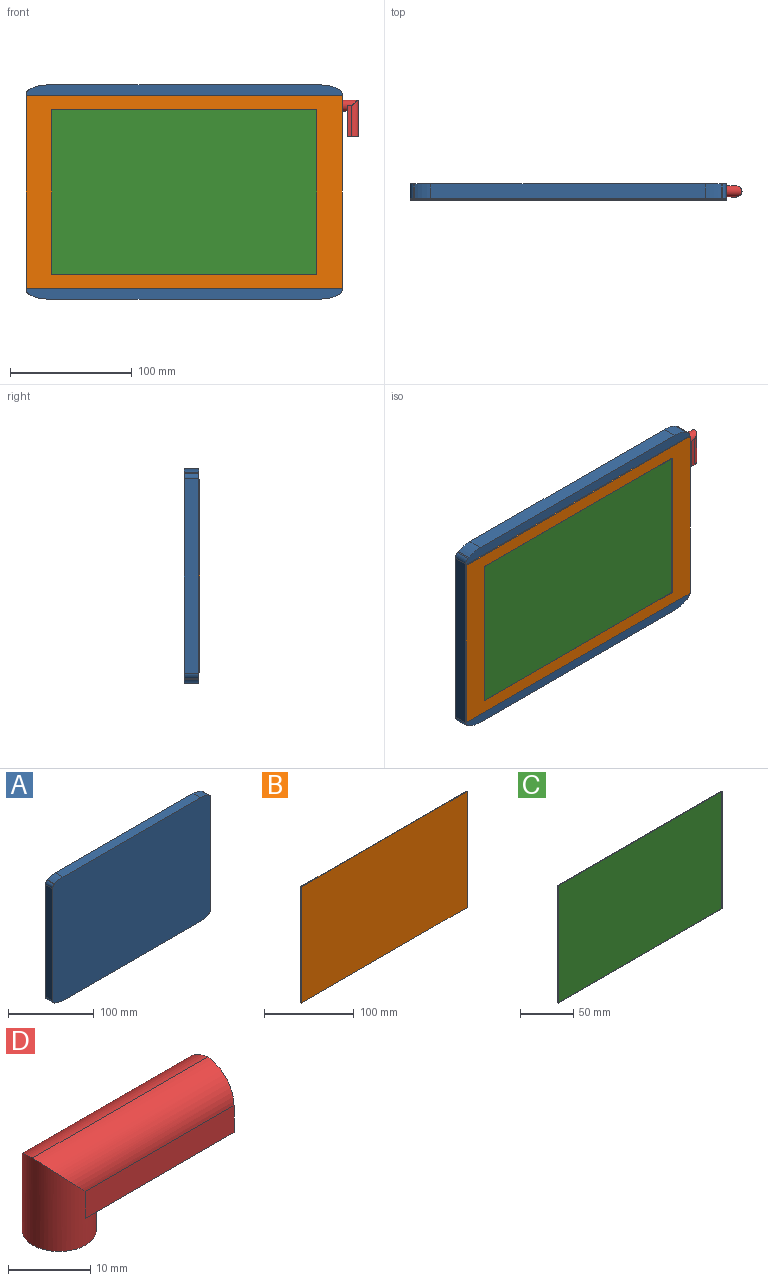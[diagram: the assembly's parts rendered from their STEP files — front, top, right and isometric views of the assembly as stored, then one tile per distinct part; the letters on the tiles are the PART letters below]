
ASSEMBLY  parts=4 mates=3
PART A: 20 faces, bbox 260x12x176 mm
  f0: plane 12x0.9mm, normal (-0.45,0,0.89), area 12.1mm2, adj f8,f9,f10,f17
  f1: plane 159.82x12mm, normal (-1,0,0), area 1917.8mm2, adj f8,f9,f10,f11
  f2: plane 12x0.9mm, normal (-0.45,0,-0.89), area 12.1mm2, adj f8,f9,f11,f14
  f3: plane 225.84x12mm, normal (0,0,-1), area 2710mm2, adj f8,f9,f14,f15
  f4: plane 12x0.9mm, normal (0.45,0,-0.89), area 12.1mm2, adj f8,f9,f12,f15
  f5: plane 159.82x12mm, normal (1,0,0), area 1909.8mm2, adj f8,f9,f12,f13,f19
  f6: plane 12x0.9mm, normal (0.45,0,0.89), area 12.1mm2, adj f8,f9,f13,f16
  f7: plane 225.84x12mm, normal (0,0,1), area 2710mm2, adj f8,f9,f16,f17
  f8: plane 260x176mm, normal (0,-1,0), area 45638.3mm2, adj f0,f1,f2,f3,f4,f5,f6,f7
  f9: plane 260x176mm, normal (0,1,0), area 45638.3mm2, adj f0,f1,f2,f3,f4,f5,f6,f7
  f10: cylinder r=5mm len=12mm, axis (0,1,0), area 66.4mm2, adj f0,f1,f8,f9
  f11: cylinder r=5mm len=12mm, axis (0,-1,0), area 66.4mm2, adj f1,f2,f8,f9
  f12: cylinder r=5mm len=12mm, axis (0,-1,0), area 66.4mm2, adj f4,f5,f8,f9
  f13: cylinder r=5mm len=12mm, axis (0,-1,0), area 66.4mm2, adj f5,f6,f8,f9
  f14: cylinder r=30mm len=13.42mm, axis (0,-1,0), area 166.9mm2, adj f2,f3,f8,f9
  f15: cylinder r=30mm len=13.42mm, axis (0,1,0), area 166.9mm2, adj f3,f4,f8,f9
  f16: cylinder r=30mm len=13.42mm, axis (0,-1,0), area 166.9mm2, adj f6,f7,f8,f9
  f17: cylinder r=30mm len=13.42mm, axis (0,-1,0), area 166.9mm2, adj f0,f7,f8,f9
  f18: cone r=0mm half-angle=59deg, axis (1,0,0), area 9.4mm2, adj f19
  f19: cylinder r=1.6mm len=10mm, axis (1,0,0), area 100.5mm2, adj f5,f18
PART B: 6 faces, bbox 260x1x158 mm
  f0: plane 260x1mm, normal (0,0,-1), area 260mm2, adj f1,f3,f4,f5
  f1: plane 158x1mm, normal (1,0,0), area 158mm2, adj f0,f2,f4,f5
  f2: plane 260x1mm, normal (0,0,1), area 260mm2, adj f1,f3,f4,f5
  f3: plane 158x1mm, normal (-1,0,0), area 158mm2, adj f0,f2,f4,f5
  f4: plane 260x158mm, normal (0,1,0), area 41080mm2, adj f0,f1,f2,f3
  f5: plane 260x158mm, normal (0,-1,0), area 41080mm2, adj f0,f1,f2,f3
PART C: 6 faces, bbox 218x0.1x135 mm
  f0: plane 218x0.1mm, normal (0,0,-1), area 21.8mm2, adj f1,f3,f4,f5
  f1: plane 135x0.1mm, normal (1,0,0), area 13.5mm2, adj f0,f2,f4,f5
  f2: plane 218x0.1mm, normal (0,0,1), area 21.8mm2, adj f1,f3,f4,f5
  f3: plane 135x0.1mm, normal (-1,0,0), area 13.5mm2, adj f0,f2,f4,f5
  f4: plane 218x135mm, normal (0,-1,0), area 29430mm2, adj f0,f1,f2,f3
  f5: plane 218x135mm, normal (0,1,0), area 29430mm2, adj f0,f1,f2,f3
PART D: 8 faces, bbox 30x9x13 mm
  f0: plane 25.5x4mm, normal (0,1,0), area 102mm2, adj f1,f4,f5,f7
  f1: cylinder r=5mm len=30mm, axis (-1,0,0), area 208.5mm2, adj f0,f3,f5,f7
  f2: plane 25.5x4mm, normal (0,-1,0), area 102mm2, adj f3,f4,f5,f7
  f3: cylinder r=5mm len=30mm, axis (1,0,0), area 208.5mm2, adj f1,f2,f5,f7
  f4: plane 25.5x9mm, normal (0,0,-1), area 197.7mm2, adj f0,f2,f5,f7
  f5: plane 9x8.98mm, normal (1,0,0), area 70.3mm2, adj f0,f1,f2,f3,f4
  f6: plane 9x9mm, normal (0,0,-1), area 63.6mm2, adj f7
  f7: cylinder r=4.5mm len=12.98mm, axis (0,0,-1), area 213.1mm2, adj f0,f1,f2,f3,f4,f6
PLACE A t=(-218.3,-114.34,-39.48)mm fixed
PLACE B t=(-218.3,-115.34,-39.48)mm
PLACE C t=(-218.3,-115.34,-39.48)mm
PLACE D rot(axis=(-0.01,1,-0.01),90deg) t=(-80.7,-115.96,21.1)mm
MATE fastened A.f8 <-> B.f4  axis (0,-1,0) through (-218.3,-126.34,-39.48)mm
MATE revolute A.f18 <-> D.f7  axis (1,0,0) through (-88.3,-120.34,31.52)mm
MATE fastened B.f5 <-> C.f5  axis (0,-1,0) through (-218.3,-127.34,-39.48)mm
